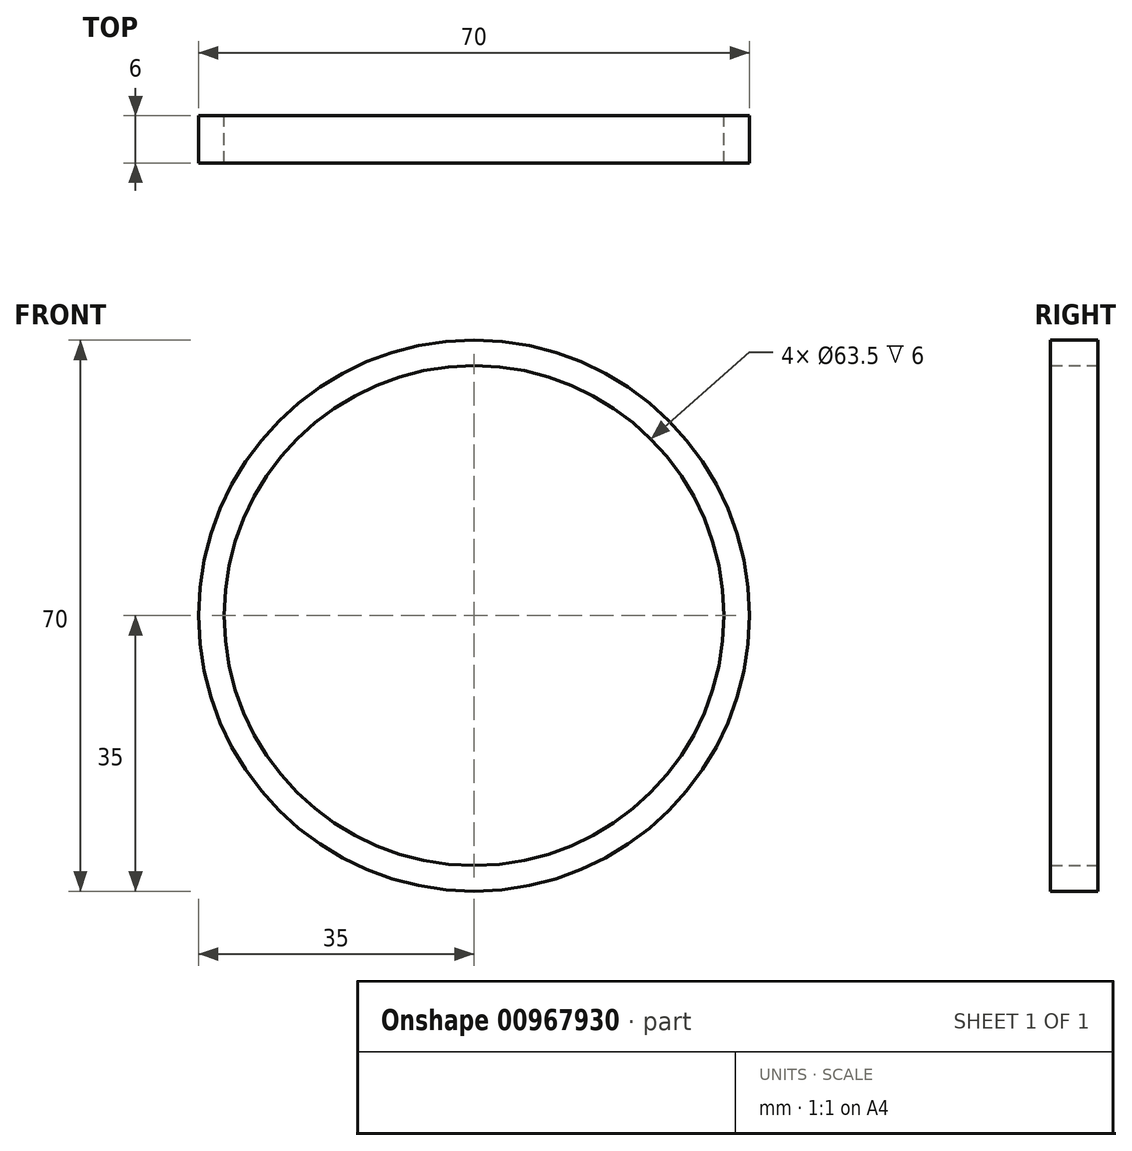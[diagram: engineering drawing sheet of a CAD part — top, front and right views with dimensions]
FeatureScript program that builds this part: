
annotation { "Feature Type Name" : "Feature", "Feature Type Description" : "" }
export const myFeature = defineFeature(function(context is Context, id is Id, definition is map)
    precondition{}
    {
        {
            var Q0;
            Q0=qCreatedBy(makeId("Front.planeOp"),FACE);
            var sketch = newSketch(context, id + "F0", { "sketchPlane" : qUnion([Q0])});
            skCircle(sketch, "E0", {"center": v(0, 0) * mm, "radius": 35 * mm});
            skCircle(sketch, "E1", {"center": v(0, 0) * mm, "radius": 31.75 * mm});
            skSolve(sketch);
        }
        {
            var Q0;
            Q0=makeQuery(id+"F0.imprint","IMPRINT",FACE,{"disambiguationData":[TD([[makeQuery(id+"F0.imprint","IMPRINT",EDGE,{"derivedFrom":sQuery(id+"F0.wireOp",EDGE,"E0")}),1.0]])]});
            extrude(context, id + "F1", {"entities" : qUnion([Q0]), "depth" : 6 * mm, "offsetDistance" : 25 * mm, "symmetric" : true});
        }
    });
